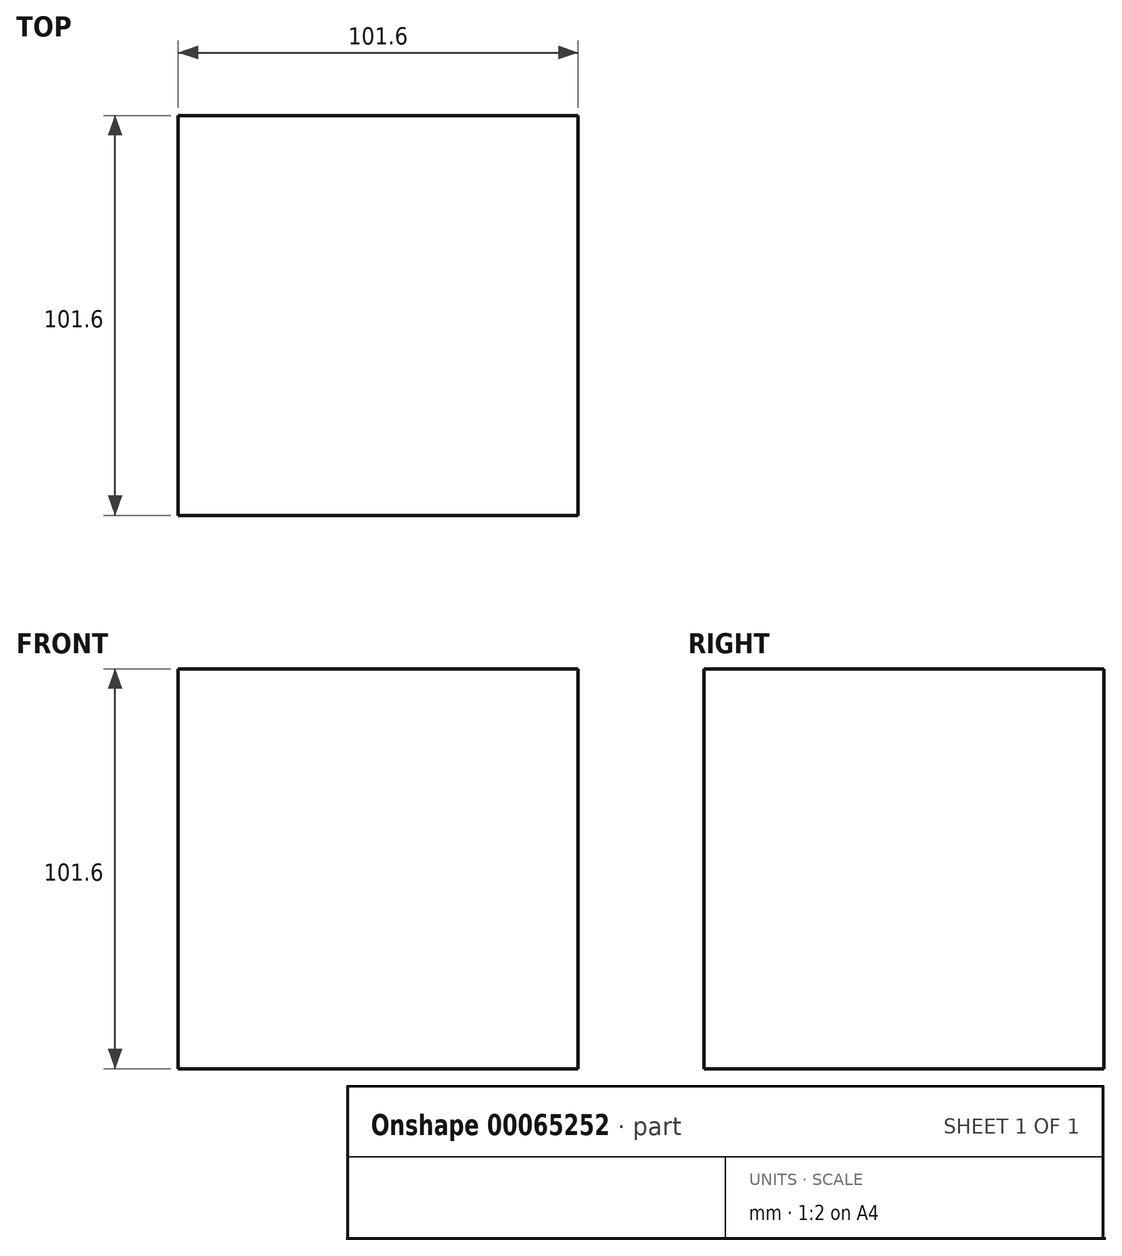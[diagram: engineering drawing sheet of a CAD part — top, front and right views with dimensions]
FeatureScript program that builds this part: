
annotation { "Feature Type Name" : "Feature", "Feature Type Description" : "" }
export const myFeature = defineFeature(function(context is Context, id is Id, definition is map)
    precondition{}
    {
        {
            var Q0;
            Q0=qCreatedBy(makeId("Top.planeOp"),FACE);
            var sketch = newSketch(context, id + "F0", { "sketchPlane" : qUnion([Q0])});
            skLineSegment(sketch, "E0.rect.bottom", {"start": v(-50.8, 50.8) * mm, "end": v(50.8, 50.8) * mm});
            skLineSegment(sketch, "E0.rect.top", {"start": v(-50.8, -50.8) * mm, "end": v(50.8, -50.8) * mm});
            skLineSegment(sketch, "E0.rect.left", {"start": v(-50.8, 50.8) * mm, "end": v(-50.8, -50.8) * mm});
            skLineSegment(sketch, "E0.rect.right", {"start": v(50.8, 50.8) * mm, "end": v(50.8, -50.8) * mm});
            skPoint(sketch, "E0.rect.middle", {"position": v(0, 0) * mm});
            skSolve(sketch);
        }
        {
            var Q0;
            Q0=makeQuery(id+"F0.imprint","IMPRINT",FACE,{"disambiguationData":[TD([[makeQuery(id+"F0.imprint","IMPRINT",EDGE,{"derivedFrom":sQuery(id+"F0.wireOp",EDGE,"E0.rect.bottom")}),-1.0]])]});
            extrude(context, id + "F1", {"entities" : qUnion([Q0]), "depth" : 101.6 * mm});
        }
    });
